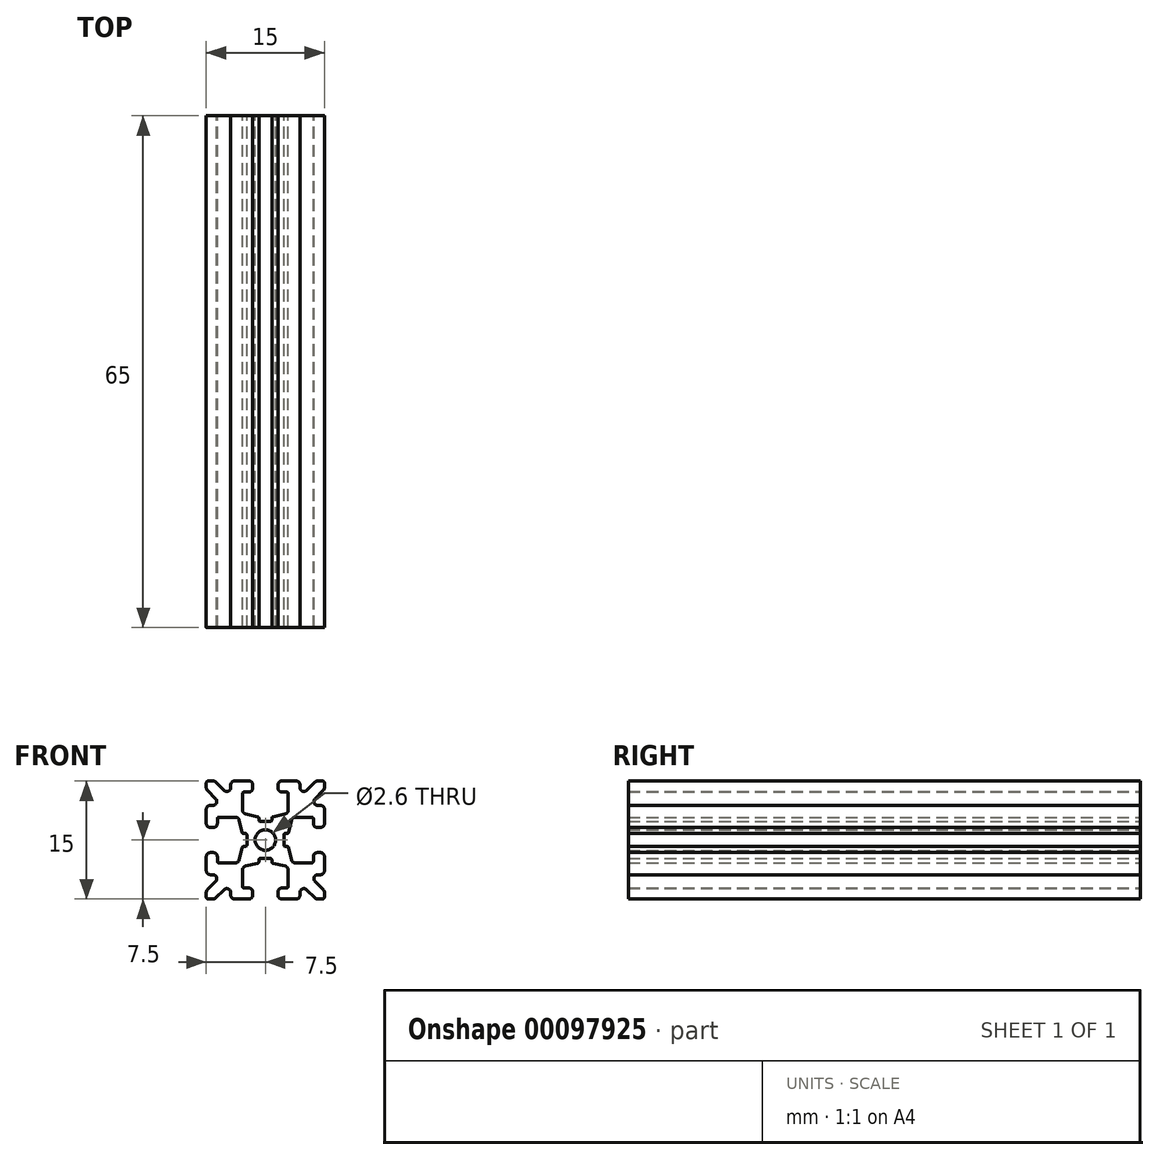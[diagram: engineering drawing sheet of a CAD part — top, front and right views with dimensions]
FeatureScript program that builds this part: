
annotation { "Feature Type Name" : "Feature", "Feature Type Description" : "" }
export const myFeature = defineFeature(function(context is Context, id is Id, definition is map)
    precondition{}
    {
        {
            var Q0;
            Q0=qCreatedBy(makeId("Front.planeOp"),FACE);
            var sketch = newSketch(context, id + "F0", { "sketchPlane" : qUnion([Q0])});
            skLineSegment(sketch, "E0.0.0", {"start": v(0.83, -2.55) * mm, "end": v(0.83, -2.77) * mm});
            skArc(sketch, "E0.0.1", {"start": v(0.83, -2.77) * mm, "mid": v(0.87, -2.9) * mm, "end": v(0.98, -2.97) * mm});
            skLineSegment(sketch, "E0.0.2", {"start": v(0.98, -2.97) * mm, "end": v(2.5, -3.31) * mm});
            skArc(sketch, "E0.0.3", {"start": v(2.5, -3.31) * mm, "mid": v(2.8, -3.49) * mm, "end": v(2.9, -3.8) * mm});
            skLineSegment(sketch, "E0.0.4", {"start": v(2.9, -3.8) * mm, "end": v(2.9, -5.9) * mm});
            skArc(sketch, "E0.0.5", {"start": v(2.9, -5.9) * mm, "mid": v(2.84, -6.04) * mm, "end": v(2.7, -6.1) * mm});
            skLineSegment(sketch, "E0.0.6", {"start": v(2.7, -6.1) * mm, "end": v(2.1, -6.1) * mm});
            skArc(sketch, "E0.0.7", {"start": v(2.1, -6.1) * mm, "mid": v(1.75, -6.25) * mm, "end": v(1.6, -6.6) * mm});
            skLineSegment(sketch, "E0.0.8", {"start": v(1.6, -6.6) * mm, "end": v(1.6, -7) * mm});
            skArc(sketch, "E0.0.9", {"start": v(1.6, -7) * mm, "mid": v(1.75, -7.35) * mm, "end": v(2.1, -7.5) * mm});
            skLineSegment(sketch, "E0.0.10", {"start": v(2.1, -7.5) * mm, "end": v(3.9, -7.5) * mm});
            skArc(sketch, "E0.0.11", {"start": v(3.9, -7.5) * mm, "mid": v(4.25, -7.35) * mm, "end": v(4.4, -7) * mm});
            skLineSegment(sketch, "E0.0.12", {"start": v(4.4, -7) * mm, "end": v(4.4, -6.67) * mm});
            skArc(sketch, "E0.0.13", {"start": v(4.4, -6.67) * mm, "mid": v(4.7, -6.2) * mm, "end": v(5.25, -6.31) * mm});
            skLineSegment(sketch, "E0.0.14", {"start": v(5.25, -6.31) * mm, "end": v(6.3, -7.35) * mm});
            skArc(sketch, "E0.0.15", {"start": v(6.3, -7.35) * mm, "mid": v(6.46, -7.46) * mm, "end": v(6.65, -7.5) * mm});
            skLineSegment(sketch, "E0.0.16", {"start": v(6.65, -7.5) * mm, "end": v(7.25, -7.5) * mm});
            skArc(sketch, "E0.0.17", {"start": v(7.25, -7.5) * mm, "mid": v(7.43, -7.43) * mm, "end": v(7.5, -7.25) * mm});
            skLineSegment(sketch, "E0.0.18", {"start": v(7.5, -7.25) * mm, "end": v(7.5, -6.65) * mm});
            skArc(sketch, "E0.0.19", {"start": v(7.5, -6.65) * mm, "mid": v(7.46, -6.46) * mm, "end": v(7.35, -6.3) * mm});
            skLineSegment(sketch, "E0.0.20", {"start": v(7.35, -6.3) * mm, "end": v(6.31, -5.25) * mm});
            skArc(sketch, "E0.0.21", {"start": v(6.31, -5.25) * mm, "mid": v(6.2, -4.7) * mm, "end": v(6.67, -4.4) * mm});
            skLineSegment(sketch, "E0.0.22", {"start": v(6.67, -4.4) * mm, "end": v(7, -4.4) * mm});
            skArc(sketch, "E0.0.23", {"start": v(7, -4.4) * mm, "mid": v(7.35, -4.25) * mm, "end": v(7.5, -3.9) * mm});
            skLineSegment(sketch, "E0.0.24", {"start": v(7.5, -3.9) * mm, "end": v(7.5, -2.1) * mm});
            skArc(sketch, "E0.0.25", {"start": v(7.5, -2.1) * mm, "mid": v(7.35, -1.75) * mm, "end": v(7, -1.6) * mm});
            skLineSegment(sketch, "E0.0.26", {"start": v(7, -1.6) * mm, "end": v(6.6, -1.6) * mm});
            skArc(sketch, "E0.0.27", {"start": v(6.6, -1.6) * mm, "mid": v(6.25, -1.75) * mm, "end": v(6.1, -2.1) * mm});
            skLineSegment(sketch, "E0.0.28", {"start": v(6.1, -2.1) * mm, "end": v(6.1, -2.7) * mm});
            skArc(sketch, "E0.0.29", {"start": v(6.1, -2.7) * mm, "mid": v(6.04, -2.84) * mm, "end": v(5.9, -2.9) * mm});
            skLineSegment(sketch, "E0.0.30", {"start": v(5.9, -2.9) * mm, "end": v(3.8, -2.9) * mm});
            skArc(sketch, "E0.0.31", {"start": v(3.8, -2.9) * mm, "mid": v(3.49, -2.8) * mm, "end": v(3.31, -2.5) * mm});
            skLineSegment(sketch, "E0.0.32", {"start": v(3.31, -2.5) * mm, "end": v(2.97, -0.98) * mm});
            skArc(sketch, "E0.0.33", {"start": v(2.97, -0.98) * mm, "mid": v(2.9, -0.87) * mm, "end": v(2.77, -0.83) * mm});
            skLineSegment(sketch, "E0.0.34", {"start": v(2.77, -0.83) * mm, "end": v(2.55, -0.83) * mm});
            skArc(sketch, "E0.0.35", {"start": v(2.55, -0.83) * mm, "mid": v(2.4, -0.77) * mm, "end": v(2.35, -0.63) * mm});
            skLineSegment(sketch, "E0.0.36", {"start": v(2.35, -0.63) * mm, "end": v(2.35, 0.63) * mm});
            skArc(sketch, "E0.0.37", {"start": v(2.35, 0.63) * mm, "mid": v(2.4, 0.77) * mm, "end": v(2.55, 0.83) * mm});
            skLineSegment(sketch, "E0.0.38", {"start": v(2.55, 0.83) * mm, "end": v(2.77, 0.83) * mm});
            skArc(sketch, "E0.0.39", {"start": v(2.77, 0.83) * mm, "mid": v(2.9, 0.87) * mm, "end": v(2.97, 0.98) * mm});
            skLineSegment(sketch, "E0.0.40", {"start": v(2.97, 0.98) * mm, "end": v(3.31, 2.5) * mm});
            skArc(sketch, "E0.0.41", {"start": v(3.31, 2.5) * mm, "mid": v(3.49, 2.8) * mm, "end": v(3.8, 2.9) * mm});
            skLineSegment(sketch, "E0.0.42", {"start": v(3.8, 2.9) * mm, "end": v(5.9, 2.9) * mm});
            skArc(sketch, "E0.0.43", {"start": v(5.9, 2.9) * mm, "mid": v(6.04, 2.84) * mm, "end": v(6.1, 2.7) * mm});
            skLineSegment(sketch, "E0.0.44", {"start": v(6.1, 2.7) * mm, "end": v(6.1, 2.1) * mm});
            skArc(sketch, "E0.0.45", {"start": v(6.1, 2.1) * mm, "mid": v(6.25, 1.75) * mm, "end": v(6.6, 1.6) * mm});
            skLineSegment(sketch, "E0.0.46", {"start": v(6.6, 1.6) * mm, "end": v(7, 1.6) * mm});
            skArc(sketch, "E0.0.47", {"start": v(7, 1.6) * mm, "mid": v(7.35, 1.75) * mm, "end": v(7.5, 2.1) * mm});
            skLineSegment(sketch, "E0.0.48", {"start": v(7.5, 2.1) * mm, "end": v(7.5, 3.9) * mm});
            skArc(sketch, "E0.0.49", {"start": v(7.5, 3.9) * mm, "mid": v(7.35, 4.25) * mm, "end": v(7, 4.4) * mm});
            skLineSegment(sketch, "E0.0.50", {"start": v(7, 4.4) * mm, "end": v(6.67, 4.4) * mm});
            skArc(sketch, "E0.0.51", {"start": v(6.67, 4.4) * mm, "mid": v(6.2, 4.7) * mm, "end": v(6.31, 5.25) * mm});
            skLineSegment(sketch, "E0.0.52", {"start": v(6.31, 5.25) * mm, "end": v(7.35, 6.3) * mm});
            skArc(sketch, "E0.0.53", {"start": v(7.35, 6.3) * mm, "mid": v(7.46, 6.46) * mm, "end": v(7.5, 6.65) * mm});
            skLineSegment(sketch, "E0.0.54", {"start": v(7.5, 6.65) * mm, "end": v(7.5, 7.25) * mm});
            skArc(sketch, "E0.0.55", {"start": v(7.5, 7.25) * mm, "mid": v(7.43, 7.43) * mm, "end": v(7.25, 7.5) * mm});
            skLineSegment(sketch, "E0.0.56", {"start": v(7.25, 7.5) * mm, "end": v(6.65, 7.5) * mm});
            skArc(sketch, "E0.0.57", {"start": v(6.65, 7.5) * mm, "mid": v(6.46, 7.46) * mm, "end": v(6.3, 7.35) * mm});
            skLineSegment(sketch, "E0.0.58", {"start": v(6.3, 7.35) * mm, "end": v(5.25, 6.31) * mm});
            skArc(sketch, "E0.0.59", {"start": v(5.25, 6.31) * mm, "mid": v(4.7, 6.2) * mm, "end": v(4.4, 6.67) * mm});
            skLineSegment(sketch, "E0.0.60", {"start": v(4.4, 6.67) * mm, "end": v(4.4, 7) * mm});
            skArc(sketch, "E0.0.61", {"start": v(4.4, 7) * mm, "mid": v(4.25, 7.35) * mm, "end": v(3.9, 7.5) * mm});
            skLineSegment(sketch, "E0.0.62", {"start": v(3.9, 7.5) * mm, "end": v(2.1, 7.5) * mm});
            skArc(sketch, "E0.0.63", {"start": v(2.1, 7.5) * mm, "mid": v(1.75, 7.35) * mm, "end": v(1.6, 7) * mm});
            skLineSegment(sketch, "E0.0.64", {"start": v(1.6, 7) * mm, "end": v(1.6, 6.6) * mm});
            skArc(sketch, "E0.0.65", {"start": v(1.6, 6.6) * mm, "mid": v(1.75, 6.25) * mm, "end": v(2.1, 6.1) * mm});
            skLineSegment(sketch, "E0.0.66", {"start": v(2.1, 6.1) * mm, "end": v(2.7, 6.1) * mm});
            skArc(sketch, "E0.0.67", {"start": v(2.7, 6.1) * mm, "mid": v(2.84, 6.04) * mm, "end": v(2.9, 5.9) * mm});
            skLineSegment(sketch, "E0.0.68", {"start": v(2.9, 5.9) * mm, "end": v(2.9, 3.8) * mm});
            skArc(sketch, "E0.0.69", {"start": v(2.9, 3.8) * mm, "mid": v(2.8, 3.49) * mm, "end": v(2.5, 3.31) * mm});
            skLineSegment(sketch, "E0.0.70", {"start": v(2.5, 3.31) * mm, "end": v(0.98, 2.97) * mm});
            skArc(sketch, "E0.0.71", {"start": v(0.98, 2.97) * mm, "mid": v(0.87, 2.9) * mm, "end": v(0.83, 2.77) * mm});
            skLineSegment(sketch, "E0.0.72", {"start": v(0.83, 2.77) * mm, "end": v(0.83, 2.55) * mm});
            skArc(sketch, "E0.0.73", {"start": v(0.83, 2.55) * mm, "mid": v(0.77, 2.4) * mm, "end": v(0.63, 2.35) * mm});
            skLineSegment(sketch, "E0.0.74", {"start": v(0.63, 2.35) * mm, "end": v(-0.63, 2.35) * mm});
            skArc(sketch, "E0.0.75", {"start": v(-0.63, 2.35) * mm, "mid": v(-0.77, 2.4) * mm, "end": v(-0.83, 2.55) * mm});
            skLineSegment(sketch, "E0.0.76", {"start": v(-0.83, 2.55) * mm, "end": v(-0.83, 2.77) * mm});
            skArc(sketch, "E0.0.77", {"start": v(-0.83, 2.77) * mm, "mid": v(-0.87, 2.9) * mm, "end": v(-0.98, 2.97) * mm});
            skLineSegment(sketch, "E0.0.78", {"start": v(-0.98, 2.97) * mm, "end": v(-2.5, 3.31) * mm});
            skArc(sketch, "E0.0.79", {"start": v(-2.5, 3.31) * mm, "mid": v(-2.8, 3.49) * mm, "end": v(-2.9, 3.8) * mm});
            skLineSegment(sketch, "E0.0.80", {"start": v(-2.9, 3.8) * mm, "end": v(-2.9, 5.9) * mm});
            skArc(sketch, "E0.0.81", {"start": v(-2.9, 5.9) * mm, "mid": v(-2.84, 6.04) * mm, "end": v(-2.7, 6.1) * mm});
            skLineSegment(sketch, "E0.0.82", {"start": v(-2.7, 6.1) * mm, "end": v(-2.1, 6.1) * mm});
            skArc(sketch, "E0.0.83", {"start": v(-2.1, 6.1) * mm, "mid": v(-1.75, 6.25) * mm, "end": v(-1.6, 6.6) * mm});
            skLineSegment(sketch, "E0.0.84", {"start": v(-1.6, 6.6) * mm, "end": v(-1.6, 7) * mm});
            skArc(sketch, "E0.0.85", {"start": v(-1.6, 7) * mm, "mid": v(-1.75, 7.35) * mm, "end": v(-2.1, 7.5) * mm});
            skLineSegment(sketch, "E0.0.86", {"start": v(-2.1, 7.5) * mm, "end": v(-3.9, 7.5) * mm});
            skArc(sketch, "E0.0.87", {"start": v(-3.9, 7.5) * mm, "mid": v(-4.25, 7.35) * mm, "end": v(-4.4, 7) * mm});
            skLineSegment(sketch, "E0.0.88", {"start": v(-4.4, 7) * mm, "end": v(-4.4, 6.67) * mm});
            skArc(sketch, "E0.0.89", {"start": v(-4.4, 6.67) * mm, "mid": v(-4.7, 6.2) * mm, "end": v(-5.25, 6.31) * mm});
            skLineSegment(sketch, "E0.0.90", {"start": v(-5.25, 6.31) * mm, "end": v(-6.3, 7.35) * mm});
            skArc(sketch, "E0.0.91", {"start": v(-6.3, 7.35) * mm, "mid": v(-6.46, 7.46) * mm, "end": v(-6.65, 7.5) * mm});
            skLineSegment(sketch, "E0.0.92", {"start": v(-6.65, 7.5) * mm, "end": v(-7.25, 7.5) * mm});
            skArc(sketch, "E0.0.93", {"start": v(-7.25, 7.5) * mm, "mid": v(-7.43, 7.43) * mm, "end": v(-7.5, 7.25) * mm});
            skLineSegment(sketch, "E0.0.94", {"start": v(-7.5, 7.25) * mm, "end": v(-7.5, 6.65) * mm});
            skArc(sketch, "E0.0.95", {"start": v(-7.5, 6.65) * mm, "mid": v(-7.46, 6.46) * mm, "end": v(-7.35, 6.3) * mm});
            skLineSegment(sketch, "E0.0.96", {"start": v(-7.35, 6.3) * mm, "end": v(-6.31, 5.25) * mm});
            skArc(sketch, "E0.0.97", {"start": v(-6.31, 5.25) * mm, "mid": v(-6.2, 4.7) * mm, "end": v(-6.67, 4.4) * mm});
            skLineSegment(sketch, "E0.0.98", {"start": v(-6.67, 4.4) * mm, "end": v(-7, 4.4) * mm});
            skArc(sketch, "E0.0.99", {"start": v(-7, 4.4) * mm, "mid": v(-7.35, 4.25) * mm, "end": v(-7.5, 3.9) * mm});
            skLineSegment(sketch, "E0.0.100", {"start": v(-7.5, 3.9) * mm, "end": v(-7.5, 2.1) * mm});
            skArc(sketch, "E0.0.101", {"start": v(-7.5, 2.1) * mm, "mid": v(-7.35, 1.75) * mm, "end": v(-7, 1.6) * mm});
            skLineSegment(sketch, "E0.0.102", {"start": v(-7, 1.6) * mm, "end": v(-6.6, 1.6) * mm});
            skArc(sketch, "E0.0.103", {"start": v(-6.6, 1.6) * mm, "mid": v(-6.25, 1.75) * mm, "end": v(-6.1, 2.1) * mm});
            skLineSegment(sketch, "E0.0.104", {"start": v(-6.1, 2.1) * mm, "end": v(-6.1, 2.7) * mm});
            skArc(sketch, "E0.0.105", {"start": v(-6.1, 2.7) * mm, "mid": v(-6.04, 2.84) * mm, "end": v(-5.9, 2.9) * mm});
            skLineSegment(sketch, "E0.0.106", {"start": v(-5.9, 2.9) * mm, "end": v(-3.8, 2.9) * mm});
            skArc(sketch, "E0.0.107", {"start": v(-3.8, 2.9) * mm, "mid": v(-3.49, 2.8) * mm, "end": v(-3.31, 2.5) * mm});
            skLineSegment(sketch, "E0.0.108", {"start": v(-3.31, 2.5) * mm, "end": v(-2.97, 0.98) * mm});
            skArc(sketch, "E0.0.109", {"start": v(-2.97, 0.98) * mm, "mid": v(-2.9, 0.87) * mm, "end": v(-2.77, 0.83) * mm});
            skLineSegment(sketch, "E0.0.110", {"start": v(-2.77, 0.83) * mm, "end": v(-2.55, 0.83) * mm});
            skArc(sketch, "E0.0.111", {"start": v(-2.55, 0.83) * mm, "mid": v(-2.4, 0.77) * mm, "end": v(-2.35, 0.63) * mm});
            skLineSegment(sketch, "E0.0.112", {"start": v(-2.35, 0.63) * mm, "end": v(-2.35, -0.63) * mm});
            skArc(sketch, "E0.0.113", {"start": v(-2.35, -0.63) * mm, "mid": v(-2.4, -0.77) * mm, "end": v(-2.55, -0.83) * mm});
            skLineSegment(sketch, "E0.0.114", {"start": v(-2.55, -0.83) * mm, "end": v(-2.77, -0.83) * mm});
            skArc(sketch, "E0.0.115", {"start": v(-2.77, -0.83) * mm, "mid": v(-2.9, -0.87) * mm, "end": v(-2.97, -0.98) * mm});
            skLineSegment(sketch, "E0.0.116", {"start": v(-2.97, -0.98) * mm, "end": v(-3.31, -2.5) * mm});
            skArc(sketch, "E0.0.117", {"start": v(-3.31, -2.5) * mm, "mid": v(-3.49, -2.8) * mm, "end": v(-3.8, -2.9) * mm});
            skLineSegment(sketch, "E0.0.118", {"start": v(-3.8, -2.9) * mm, "end": v(-5.9, -2.9) * mm});
            skArc(sketch, "E0.0.119", {"start": v(-5.9, -2.9) * mm, "mid": v(-6.04, -2.84) * mm, "end": v(-6.1, -2.7) * mm});
            skLineSegment(sketch, "E0.0.120", {"start": v(-6.1, -2.7) * mm, "end": v(-6.1, -2.1) * mm});
            skArc(sketch, "E0.0.121", {"start": v(-6.1, -2.1) * mm, "mid": v(-6.25, -1.75) * mm, "end": v(-6.6, -1.6) * mm});
            skLineSegment(sketch, "E0.0.122", {"start": v(-6.6, -1.6) * mm, "end": v(-7, -1.6) * mm});
            skArc(sketch, "E0.0.123", {"start": v(-7, -1.6) * mm, "mid": v(-7.35, -1.75) * mm, "end": v(-7.5, -2.1) * mm});
            skLineSegment(sketch, "E0.0.124", {"start": v(-7.5, -2.1) * mm, "end": v(-7.5, -3.9) * mm});
            skArc(sketch, "E0.0.125", {"start": v(-7.5, -3.9) * mm, "mid": v(-7.35, -4.25) * mm, "end": v(-7, -4.4) * mm});
            skLineSegment(sketch, "E0.0.126", {"start": v(-7, -4.4) * mm, "end": v(-6.67, -4.4) * mm});
            skArc(sketch, "E0.0.127", {"start": v(-6.67, -4.4) * mm, "mid": v(-6.2, -4.7) * mm, "end": v(-6.31, -5.25) * mm});
            skLineSegment(sketch, "E0.0.128", {"start": v(-6.31, -5.25) * mm, "end": v(-7.35, -6.3) * mm});
            skArc(sketch, "E0.0.129", {"start": v(-7.35, -6.3) * mm, "mid": v(-7.46, -6.46) * mm, "end": v(-7.5, -6.65) * mm});
            skLineSegment(sketch, "E0.0.130", {"start": v(-7.5, -6.65) * mm, "end": v(-7.5, -7.25) * mm});
            skArc(sketch, "E0.0.131", {"start": v(-7.5, -7.25) * mm, "mid": v(-7.43, -7.43) * mm, "end": v(-7.25, -7.5) * mm});
            skLineSegment(sketch, "E0.0.132", {"start": v(-7.25, -7.5) * mm, "end": v(-6.65, -7.5) * mm});
            skArc(sketch, "E0.0.133", {"start": v(-6.65, -7.5) * mm, "mid": v(-6.46, -7.46) * mm, "end": v(-6.3, -7.35) * mm});
            skLineSegment(sketch, "E0.0.134", {"start": v(-6.3, -7.35) * mm, "end": v(-5.25, -6.31) * mm});
            skArc(sketch, "E0.0.135", {"start": v(-5.25, -6.31) * mm, "mid": v(-4.7, -6.2) * mm, "end": v(-4.4, -6.67) * mm});
            skLineSegment(sketch, "E0.0.136", {"start": v(-4.4, -6.67) * mm, "end": v(-4.4, -7) * mm});
            skArc(sketch, "E0.0.137", {"start": v(-4.4, -7) * mm, "mid": v(-4.25, -7.35) * mm, "end": v(-3.9, -7.5) * mm});
            skLineSegment(sketch, "E0.0.138", {"start": v(-3.9, -7.5) * mm, "end": v(-2.1, -7.5) * mm});
            skArc(sketch, "E0.0.139", {"start": v(-2.1, -7.5) * mm, "mid": v(-1.75, -7.35) * mm, "end": v(-1.6, -7) * mm});
            skLineSegment(sketch, "E0.0.140", {"start": v(-1.6, -7) * mm, "end": v(-1.6, -6.6) * mm});
            skArc(sketch, "E0.0.141", {"start": v(-1.6, -6.6) * mm, "mid": v(-1.75, -6.25) * mm, "end": v(-2.1, -6.1) * mm});
            skLineSegment(sketch, "E0.0.142", {"start": v(-2.1, -6.1) * mm, "end": v(-2.7, -6.1) * mm});
            skArc(sketch, "E0.0.143", {"start": v(-2.7, -6.1) * mm, "mid": v(-2.84, -6.04) * mm, "end": v(-2.9, -5.9) * mm});
            skLineSegment(sketch, "E0.0.144", {"start": v(-2.9, -5.9) * mm, "end": v(-2.9, -3.8) * mm});
            skArc(sketch, "E0.0.145", {"start": v(-2.9, -3.8) * mm, "mid": v(-2.8, -3.49) * mm, "end": v(-2.5, -3.31) * mm});
            skLineSegment(sketch, "E0.0.146", {"start": v(-2.5, -3.31) * mm, "end": v(-0.98, -2.97) * mm});
            skArc(sketch, "E0.0.147", {"start": v(-0.98, -2.97) * mm, "mid": v(-0.87, -2.9) * mm, "end": v(-0.83, -2.77) * mm});
            skLineSegment(sketch, "E0.0.148", {"start": v(-0.83, -2.77) * mm, "end": v(-0.83, -2.55) * mm});
            skArc(sketch, "E0.0.149", {"start": v(-0.83, -2.55) * mm, "mid": v(-0.77, -2.4) * mm, "end": v(-0.63, -2.35) * mm});
            skLineSegment(sketch, "E0.0.150", {"start": v(-0.63, -2.35) * mm, "end": v(0.63, -2.35) * mm});
            skArc(sketch, "E0.0.151", {"start": v(0.63, -2.35) * mm, "mid": v(0.77, -2.4) * mm, "end": v(0.83, -2.55) * mm});
            skPoint(sketch, "E1", {"position": v(0, 0) * mm});
            skPoint(sketch, "E1.positionSnap0", {"position": v(0, 2.35) * mm});
            skPoint(sketch, "E1.positionSnap1", {"position": v(2.35, 0) * mm});
            skCircle(sketch, "E2", {"center": v(0, 0) * mm, "radius": 1.3 * mm});
            skSolve(sketch);
        }
        {
            var Q0;
            Q0=makeQuery(id+"F0.imprint","IMPRINT",FACE,{"disambiguationData":[TD([[makeQuery(id+"F0.imprint","IMPRINT",EDGE,{"derivedFrom":sQuery(id+"F0.wireOp",EDGE,"E0.0.0")}),1.0]])]});
            extrude(context, id + "F1", {"entities" : qUnion([Q0]), "endBound" : BoundingType.SYMMETRIC, "depth" : 65 * mm});
        }
    });
